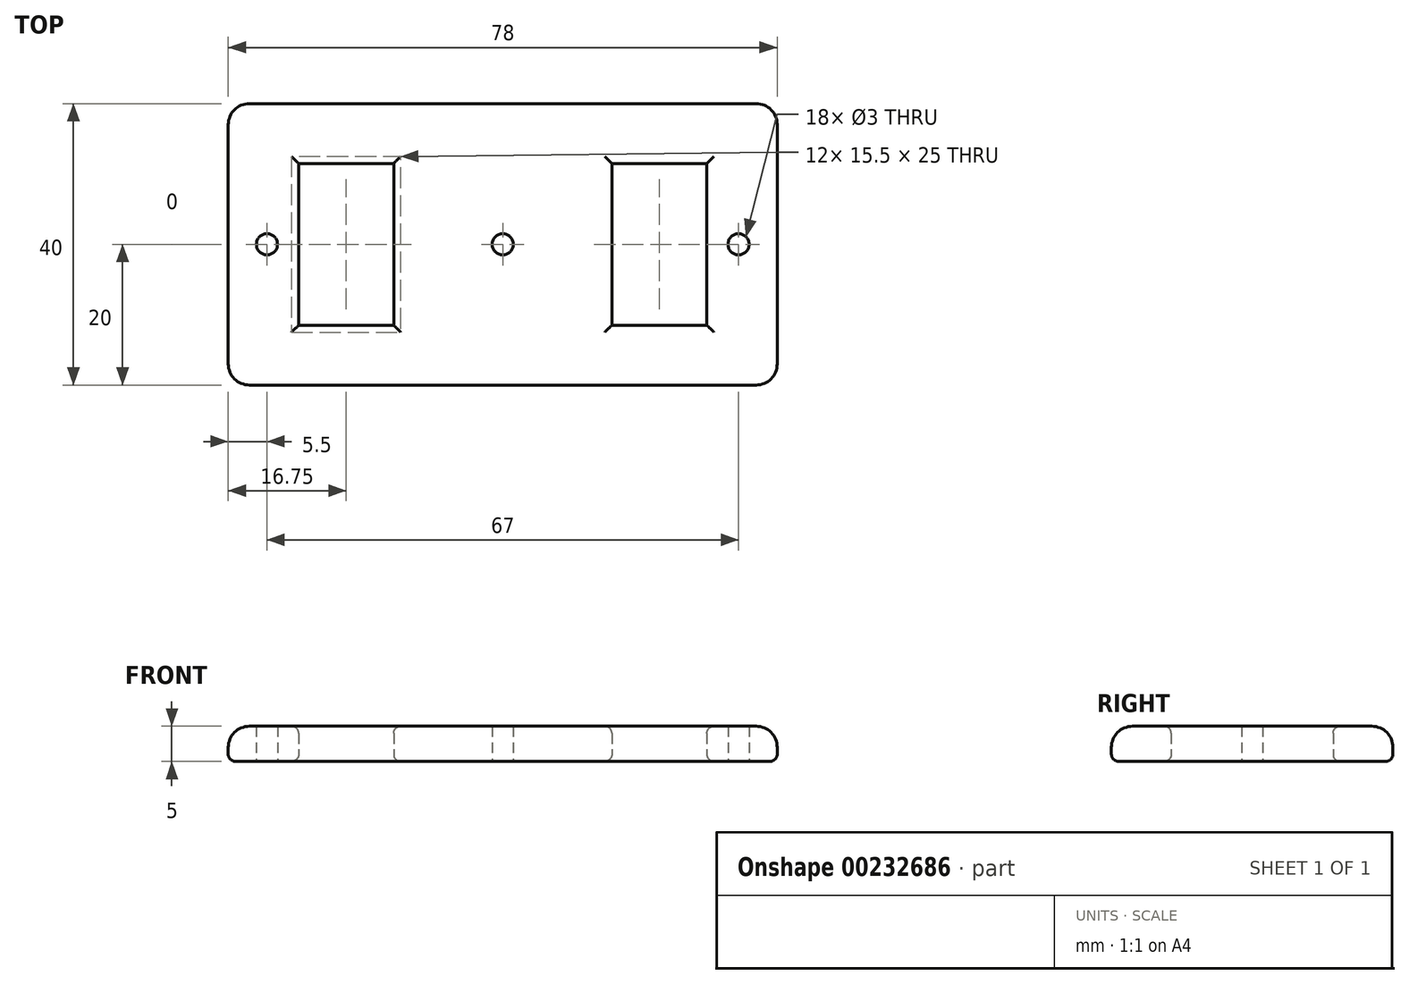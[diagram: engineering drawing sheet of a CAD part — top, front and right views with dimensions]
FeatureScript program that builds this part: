
annotation { "Feature Type Name" : "Feature", "Feature Type Description" : "" }
export const myFeature = defineFeature(function(context is Context, id is Id, definition is map)
    precondition{}
    {
        {
            var Q0;
            Q0=qCreatedBy(makeId("Top.planeOp"),FACE);
            var sketch = newSketch(context, id + "F0", { "sketchPlane" : qUnion([Q0])});
            skLineSegment(sketch, "E0.bottom", {"start": v(-39, 20) * mm, "end": v(0, 20) * mm});
            skLineSegment(sketch, "E0.top", {"start": v(-39, -20) * mm, "end": v(39, -20) * mm});
            skLineSegment(sketch, "E0.left", {"start": v(-39, 20) * mm, "end": v(-39, -20) * mm});
            skLineSegment(sketch, "E0.right", {"start": v(39, 20) * mm, "end": v(39, 0) * mm});
            skLineSegment(sketch, "E1", {"start": v(0, 73.35) * mm, "end": v(0, -33.35) * mm, "construction": true});
            skLineSegment(sketch, "E2", {"start": v(-40.36, 0) * mm, "end": v(118.36, 0) * mm, "construction": true});
            skLineSegment(sketch, "E3.bottom", {"start": v(-29, 11.5) * mm, "end": v(-15.5, 11.5) * mm});
            skLineSegment(sketch, "E3.top", {"start": v(-29, -11.5) * mm, "end": v(-15.5, -11.5) * mm});
            skLineSegment(sketch, "E3.left", {"start": v(-29, 11.5) * mm, "end": v(-29, -11.5) * mm});
            skLineSegment(sketch, "E3.right", {"start": v(-15.5, 11.5) * mm, "end": v(-15.5, -11.5) * mm});
            skLineSegment(sketch, "E4.MirrorCS", {"start": v(29, 11.5) * mm, "end": v(29, 0) * mm});
            skLineSegment(sketch, "E5.MirrorCS", {"start": v(29, 11.5) * mm, "end": v(15.5, 11.5) * mm});
            skLineSegment(sketch, "E6.MirrorCS", {"start": v(15.5, 11.5) * mm, "end": v(15.5, -11.5) * mm});
            skLineSegment(sketch, "E7.MirrorCS", {"start": v(29, -11.5) * mm, "end": v(15.5, -11.5) * mm});
            skCircle(sketch, "E8", {"center": v(-33.5, 0) * mm, "radius": 1.5 * mm});
            skCircle(sketch, "E9", {"center": v(0, 0) * mm, "radius": 1.5 * mm});
            skCircle(sketch, "E10.MirrorC", {"center": v(33.5, 0) * mm, "radius": 1.5 * mm});
            skLineSegment(sketch, "E11", {"start": v(0, 20) * mm, "end": v(39, 20) * mm});
            skLineSegment(sketch, "E12", {"start": v(39, 0) * mm, "end": v(39, -20) * mm});
            skLineSegment(sketch, "E13", {"start": v(29, 0) * mm, "end": v(29, -11.5) * mm});
            skSolve(sketch);
        }
        {
            var Q0;
            Q0=makeQuery(id+"F0.imprint","IMPRINT",FACE,{"disambiguationData":[TD([[makeQuery(id+"F0.imprint","IMPRINT",EDGE,{"derivedFrom":sQuery(id+"F0.wireOp",EDGE,"E0.bottom")}),-1.0]])]});
            extrude(context, id + "F1", {"entities" : qUnion([Q0]), "depth" : 5 * mm});
        }
        {
            var Q0;
            Q0=makeQuery(id+"F1.opExtrude","CAP_EDGE",EDGE,{"disambiguationData":[OSD([sQuery(id+"F0.wireOp",EDGE,"E0.bottom")])],"isStart":false});
            var Q1;
            Q1=makeQuery(id+"F1.opExtrude","CAP_EDGE",EDGE,{"disambiguationData":[OSD([sQuery(id+"F0.wireOp",EDGE,"E0.left")])],"isStart":false});
            var Q2;
            Q2=makeQuery(id+"F1.opExtrude","CAP_EDGE",EDGE,{"disambiguationData":[OSD([sQuery(id+"F0.wireOp",EDGE,"E0.top")])],"isStart":false});
            var Q3;
            Q3=makeQuery(id+"F1.opExtrude","CAP_EDGE",EDGE,{"disambiguationData":[OSD([sQuery(id+"F0.wireOp",EDGE,"E0.right")])],"isStart":false});
            var Q4;
            Q4=makeQuery(id+"F1.opExtrude","SWEPT_EDGE",EDGE,{"disambiguationData":[OSD([sQuery(id+"F0.wireOp",EDGE,"E0.top"),sQuery(id+"F0.wireOp",EDGE,"E0.left")])]});
            var Q5;
            Q5=makeQuery(id+"F1.opExtrude","SWEPT_EDGE",EDGE,{"disambiguationData":[OSD([sQuery(id+"F0.wireOp",EDGE,"E0.bottom"),sQuery(id+"F0.wireOp",EDGE,"E0.left")])]});
            var Q6;
            Q6=makeQuery(id+"F1.opExtrude","SWEPT_EDGE",EDGE,{"disambiguationData":[OSD([sQuery(id+"F0.wireOp",EDGE,"E0.right"),sQuery(id+"F0.wireOp",EDGE,"E11")])]});
            var Q7;
            Q7=makeQuery(id+"F1.opExtrude","SWEPT_EDGE",EDGE,{"disambiguationData":[OSD([sQuery(id+"F0.wireOp",EDGE,"E0.top"),sQuery(id+"F0.wireOp",EDGE,"E12")])]});
            fillet(context, id + "F2", {"entities" : qUnion([Q0, Q1, Q2, Q3, Q4, Q5, Q6, Q7]), "radius" : 3 * mm, "tangentPropagation" : true, "allowEdgeOverflow" : false});
        }
        {
            var Q0;
            Q0=makeQuery(id+"F1.opExtrude","CAP_EDGE",EDGE,{"disambiguationData":[OSD([sQuery(id+"F0.wireOp",EDGE,"E0.top")])],"isStart":true});
            fillet(context, id + "F3", {"entities" : qUnion([Q0]), "radius" : 1 * mm, "tangentPropagation" : true, "allowEdgeOverflow" : false});
        }
        {
            var Q0;
            Q0=makeQuery(id+"F1.opExtrude","CAP_EDGE",EDGE,{"disambiguationData":[OSD([sQuery(id+"F0.wireOp",EDGE,"E3.top")])],"isStart":false});
            var Q1;
            Q1=makeQuery(id+"F1.opExtrude","CAP_EDGE",EDGE,{"disambiguationData":[OSD([sQuery(id+"F0.wireOp",EDGE,"E3.right")])],"isStart":false});
            var Q2;
            Q2=makeQuery(id+"F1.opExtrude","CAP_EDGE",EDGE,{"disambiguationData":[OSD([sQuery(id+"F0.wireOp",EDGE,"E3.bottom")])],"isStart":false});
            var Q3;
            Q3=makeQuery(id+"F1.opExtrude","CAP_EDGE",EDGE,{"disambiguationData":[OSD([sQuery(id+"F0.wireOp",EDGE,"E3.left")])],"isStart":false});
            var Q4;
            Q4=makeQuery(id+"F1.opExtrude","CAP_EDGE",EDGE,{"disambiguationData":[OSD([sQuery(id+"F0.wireOp",EDGE,"E6.MirrorCS")])],"isStart":false});
            var Q5;
            Q5=makeQuery(id+"F1.opExtrude","CAP_EDGE",EDGE,{"disambiguationData":[OSD([sQuery(id+"F0.wireOp",EDGE,"E5.MirrorCS")])],"isStart":false});
            var Q6;
            Q6=makeQuery(id+"F1.opExtrude","CAP_EDGE",EDGE,{"disambiguationData":[OSD([sQuery(id+"F0.wireOp",EDGE,"E4.MirrorCS"),sQuery(id+"F0.wireOp",EDGE,"E13")])],"isStart":false});
            var Q7;
            Q7=makeQuery(id+"F1.opExtrude","CAP_EDGE",EDGE,{"disambiguationData":[OSD([sQuery(id+"F0.wireOp",EDGE,"E7.MirrorCS")])],"isStart":false});
            var Q8;
            Q8=makeQuery(id+"F1.opExtrude","CAP_EDGE",EDGE,{"disambiguationData":[OSD([sQuery(id+"F0.wireOp",EDGE,"E3.left")])],"isStart":true});
            var Q9;
            Q9=makeQuery(id+"F1.opExtrude","CAP_EDGE",EDGE,{"disambiguationData":[OSD([sQuery(id+"F0.wireOp",EDGE,"E3.right")])],"isStart":true});
            var Q10;
            Q10=makeQuery(id+"F1.opExtrude","CAP_EDGE",EDGE,{"disambiguationData":[OSD([sQuery(id+"F0.wireOp",EDGE,"E3.bottom")])],"isStart":true});
            var Q11;
            Q11=makeQuery(id+"F1.opExtrude","CAP_EDGE",EDGE,{"disambiguationData":[OSD([sQuery(id+"F0.wireOp",EDGE,"E3.top")])],"isStart":true});
            var Q12;
            Q12=makeQuery(id+"F1.opExtrude","CAP_EDGE",EDGE,{"disambiguationData":[OSD([sQuery(id+"F0.wireOp",EDGE,"E7.MirrorCS")])],"isStart":true});
            var Q13;
            Q13=makeQuery(id+"F1.opExtrude","CAP_EDGE",EDGE,{"disambiguationData":[OSD([sQuery(id+"F0.wireOp",EDGE,"E4.MirrorCS"),sQuery(id+"F0.wireOp",EDGE,"E13")])],"isStart":true});
            var Q14;
            Q14=makeQuery(id+"F1.opExtrude","CAP_EDGE",EDGE,{"disambiguationData":[OSD([sQuery(id+"F0.wireOp",EDGE,"E5.MirrorCS")])],"isStart":true});
            var Q15;
            Q15=makeQuery(id+"F1.opExtrude","CAP_EDGE",EDGE,{"disambiguationData":[OSD([sQuery(id+"F0.wireOp",EDGE,"E6.MirrorCS")])],"isStart":true});
            fillet(context, id + "F4", {"entities" : qUnion([Q0, Q1, Q2, Q3, Q4, Q5, Q6, Q7, Q8, Q9, Q10, Q11, Q12, Q13, Q14, Q15]), "radius" : 1 * mm, "tangentPropagation" : true, "allowEdgeOverflow" : false});
        }
    });
